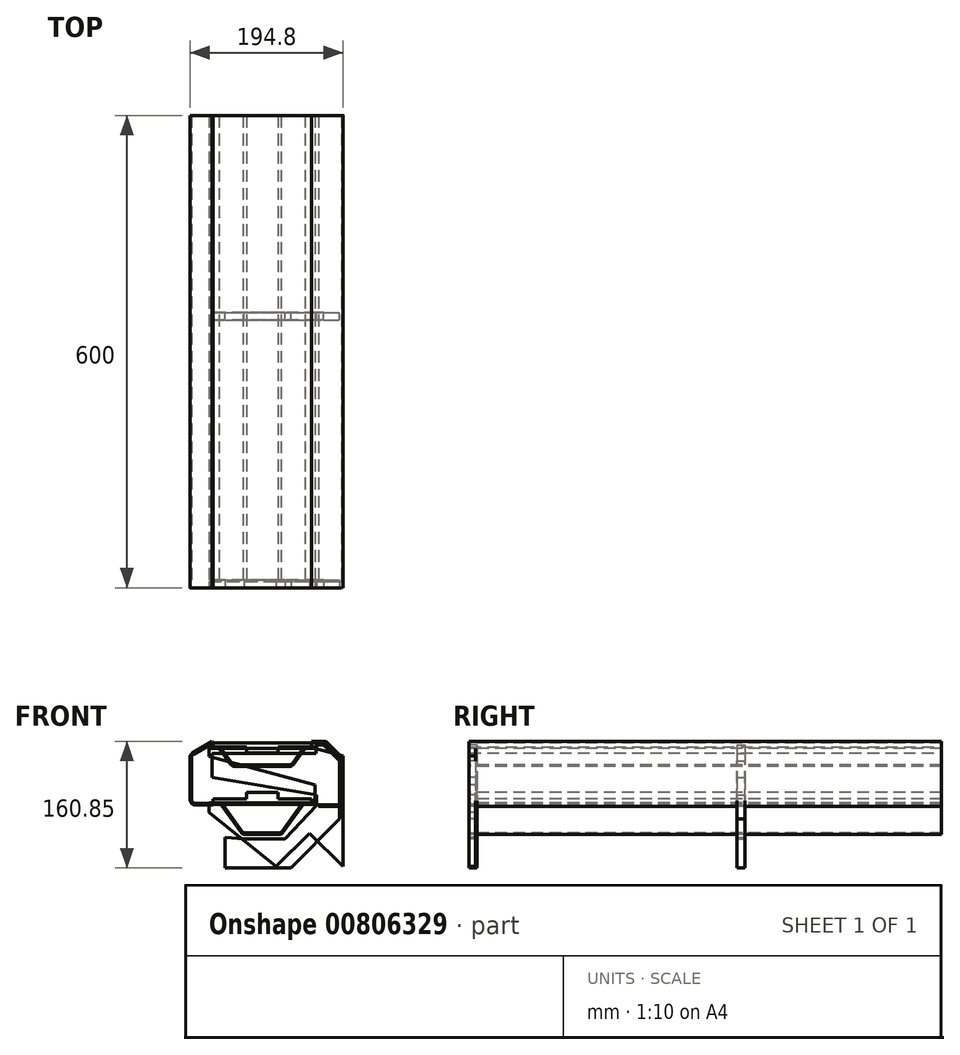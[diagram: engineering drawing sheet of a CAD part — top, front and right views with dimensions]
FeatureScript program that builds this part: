
annotation { "Feature Type Name" : "Feature", "Feature Type Description" : "" }
export const myFeature = defineFeature(function(context is Context, id is Id, definition is map)
    precondition{}
    {
        {
            var Q0;
            Q0=qCreatedBy(makeId("Front.planeOp"),FACE);
            var sketch = newSketch(context, id + "F0", { "sketchPlane" : qUnion([Q0])});
            skLineSegment(sketch, "E0.bottom", {"start": v(62.5, 2.5) * mm, "end": v(-62.5, 2.5) * mm});
            skLineSegment(sketch, "E0.top", {"start": v(62.5, -2.5) * mm, "end": v(20, -2.5) * mm});
            skLineSegment(sketch, "E0.left", {"start": v(62.5, 2.5) * mm, "end": v(62.5, -2.5) * mm});
            skLineSegment(sketch, "E0.right", {"start": v(-62.5, 2.5) * mm, "end": v(-62.5, -2.5) * mm});
            skPoint(sketch, "E0.middle", {"position": v(0, 0) * mm});
            skLineSegment(sketch, "E1.top", {"start": v(20, -10.5) * mm, "end": v(-20, -10.5) * mm});
            skLineSegment(sketch, "E1.left", {"start": v(20, -2.5) * mm, "end": v(20, -10.5) * mm});
            skLineSegment(sketch, "E1.right", {"start": v(-20, -2.5) * mm, "end": v(-20, -10.5) * mm});
            skPoint(sketch, "E1.middle", {"position": v(0, -6.5) * mm});
            skLineSegment(sketch, "E2.trimOffspring", {"start": v(-20, -2.5) * mm, "end": v(-62.5, -2.5) * mm});
            skSolve(sketch);
        }
        {
            var Q0;
            Q0 = qSketchRegion(id + "F0", true);
            extrude(context, id + "F1", {"entities" : qUnion([Q0]), "depth" : 600 * mm, "offsetDistance" : 25 * mm});
        }
        {
            var Q0;
            Q0=makeQuery(id+"F1.opExtrude","CAP_FACE",FACE,{"disambiguationData":[OSD([sQuery(id+"F0.wireOp",EDGE,"E0.bottom"),sQuery(id+"F0.wireOp",EDGE,"E0.top"),sQuery(id+"F0.wireOp",EDGE,"E0.left"),sQuery(id+"F0.wireOp",EDGE,"E0.right"),sQuery(id+"F0.wireOp",EDGE,"E1.top"),sQuery(id+"F0.wireOp",EDGE,"E1.left"),sQuery(id+"F0.wireOp",EDGE,"E1.right"),sQuery(id+"F0.wireOp",EDGE,"E2.trimOffspring")])],"isStart":false});
            var sketch = newSketch(context, id + "F2", { "sketchPlane" : qUnion([Q0])});
            skLineSegment(sketch, "E3.bottom", {"start": v(62.5, -68.5) * mm, "end": v(-62.5, -68.5) * mm});
            skLineSegment(sketch, "E3.top", {"start": v(62.5, -73.5) * mm, "end": v(-62.5, -73.5) * mm});
            skLineSegment(sketch, "E3.left", {"start": v(62.5, -68.5) * mm, "end": v(62.5, -73.5) * mm});
            skLineSegment(sketch, "E3.right", {"start": v(-62.5, -68.5) * mm, "end": v(-62.5, -73.5) * mm});
            skPoint(sketch, "E3.middle", {"position": v(0, -71) * mm});
            skLineSegment(sketch, "E4.bottom", {"start": v(20, -68.5) * mm, "end": v(-20, -68.5) * mm});
            skLineSegment(sketch, "E4.top", {"start": v(20, -60.5) * mm, "end": v(-20, -60.5) * mm});
            skLineSegment(sketch, "E4.left", {"start": v(20, -68.5) * mm, "end": v(20, -60.5) * mm});
            skLineSegment(sketch, "E4.right", {"start": v(-20, -68.5) * mm, "end": v(-20, -60.5) * mm});
            skPoint(sketch, "E4.middle", {"position": v(0, -64.5) * mm});
            skSolve(sketch);
        }
        {
            var Q0;
            Q0 = qSketchRegion(id + "F2", true);
            extrude(context, id + "F3", {"entities" : qUnion([Q0]), "oppositeDirection" : true, "depth" : 600 * mm, "offsetDistance" : 25 * mm});
        }
        {
            var Q0;
            Q0=makeQuery(id+"F3.opExtrude","CAP_FACE",FACE,{"disambiguationData":[OSD([sQuery(id+"F2.wireOp",EDGE,"E3.bottom"),sQuery(id+"F2.wireOp",EDGE,"E3.top"),sQuery(id+"F2.wireOp",EDGE,"E3.left"),sQuery(id+"F2.wireOp",EDGE,"E3.right"),sQuery(id+"F2.wireOp",EDGE,"E4.top"),sQuery(id+"F2.wireOp",EDGE,"E4.left"),sQuery(id+"F2.wireOp",EDGE,"E4.right")])],"isStart":true});
            var sketch = newSketch(context, id + "F4", { "sketchPlane" : qUnion([Q0])});
            skLineSegment(sketch, "E5", {"start": v(-67.5, -4.5) * mm, "end": v(-67.5, -14.5) * mm});
            skLineSegment(sketch, "E6", {"start": v(-67.5, -14.5) * mm, "end": v(67.5, -50.67) * mm});
            skLineSegment(sketch, "E7", {"start": v(-67.5, -75.5) * mm, "end": v(-67.5, -85.5) * mm});
            skLineSegment(sketch, "E8", {"start": v(67.5, -75.5) * mm, "end": v(67.5, -50.67) * mm});
            skLineSegment(sketch, "E9", {"start": v(-67.5, -75.5) * mm, "end": v(67.5, -75.5) * mm});
            skLineSegment(sketch, "E10", {"start": v(-67.5, -4.5) * mm, "end": v(67.5, -4.5) * mm});
            skLineSegment(sketch, "E11", {"start": v(67.5, -4.5) * mm, "end": v(102.5, -13.88) * mm});
            skCircle(sketch, "E12.cCircle", {"center": v(60.07, -154.62) * mm, "radius": 30 * mm, "construction": true});
            skLineSegment(sketch, "E12.0", {"start": v(17.65, -154.62) * mm, "end": v(60.07, -112.2) * mm});
            skLineSegment(sketch, "E12.1", {"start": v(60.07, -112.2) * mm, "end": v(102.5, -154.62) * mm});
            skLineSegment(sketch, "E12.2", {"start": v(102.5, -154.62) * mm, "end": v(60.07, -197.05) * mm});
            skLineSegment(sketch, "E12.3", {"start": v(60.07, -197.05) * mm, "end": v(17.65, -154.62) * mm});
            skPoint(sketch, "E12.0.midPoint", {"position": v(38.86, -133.41) * mm});
            skLineSegment(sketch, "E13", {"start": v(102.5, -13.88) * mm, "end": v(102.5, -154.62) * mm});
            skLineSegment(sketch, "E14", {"start": v(17.65, -154.62) * mm, "end": v(-67.5, -85.5) * mm});
            skSolve(sketch);
        }
        {
            var Q0;
            Q0=makeQuery(id+"F4.imprint","IMPRINT",FACE,{"disambiguationData":[TD([[makeQuery(id+"F4.imprint","IMPRINT",EDGE,{"derivedFrom":sQuery(id+"F4.wireOp",EDGE,"E5")}),1.0]])]});
            extrude(context, id + "F5", {"entities" : qUnion([Q0]), "oppositeDirection" : true, "depth" : 8 * mm, "offsetDistance" : 25 * mm});
        }
        {
            var Q0;
            Q0=makeQuery(id+"F3.opExtrude","CAP_FACE",FACE,{"disambiguationData":[OSD([sQuery(id+"F2.wireOp",EDGE,"E3.bottom"),sQuery(id+"F2.wireOp",EDGE,"E3.top"),sQuery(id+"F2.wireOp",EDGE,"E3.left"),sQuery(id+"F2.wireOp",EDGE,"E3.right"),sQuery(id+"F2.wireOp",EDGE,"E4.top"),sQuery(id+"F2.wireOp",EDGE,"E4.left"),sQuery(id+"F2.wireOp",EDGE,"E4.right")])],"isStart":true});
            var sketch = newSketch(context, id + "F6", { "sketchPlane" : qUnion([Q0])});
            skLineSegment(sketch, "E15", {"start": v(-67.5, -73.5) * mm, "end": v(-67.5, -75.5) * mm});
            skLineSegment(sketch, "E16", {"start": v(-67.5, -75.5) * mm, "end": v(-54.54, -75.5) * mm});
            skLineSegment(sketch, "E17", {"start": v(-51.3, -77.15) * mm, "end": v(-26.2, -111.85) * mm});
            skLineSegment(sketch, "E18", {"start": v(-22.96, -113.5) * mm, "end": v(0, -113.5) * mm});
            skLineSegment(sketch, "E19", {"start": v(0, -113.5) * mm, "end": v(0, -98.02) * mm, "construction": true});
            skLineSegment(sketch, "E20.MirrorCS", {"start": v(67.5, -73.5) * mm, "end": v(67.5, -75.5) * mm});
            skLineSegment(sketch, "E21.MirrorCS", {"start": v(67.5, -75.5) * mm, "end": v(54.54, -75.5) * mm});
            skLineSegment(sketch, "E22.MirrorCS", {"start": v(51.3, -77.15) * mm, "end": v(26.2, -111.85) * mm});
            skLineSegment(sketch, "E23.MirrorCS", {"start": v(22.96, -113.5) * mm, "end": v(0, -113.5) * mm});
            skPoint(sketch, "E24.visualSharp", {"position": v(-25, -113.5) * mm});
            skArc(sketch, "E24.filletArc", {"start": v(-26.2, -111.85) * mm, "mid": v(-24.78, -113.06) * mm, "end": v(-22.96, -113.5) * mm});
            skPoint(sketch, "E25.visualSharp", {"position": v(25, -113.5) * mm});
            skArc(sketch, "E25.filletArc", {"start": v(22.96, -113.5) * mm, "mid": v(24.78, -113.06) * mm, "end": v(26.2, -111.85) * mm});
            skPoint(sketch, "E26.visualSharp", {"position": v(52.5, -75.5) * mm});
            skArc(sketch, "E26.filletArc", {"start": v(54.54, -75.5) * mm, "mid": v(52.72, -75.94) * mm, "end": v(51.3, -77.15) * mm});
            skPoint(sketch, "E27.visualSharp", {"position": v(-52.5, -75.5) * mm});
            skArc(sketch, "E27.filletArc", {"start": v(-51.3, -77.15) * mm, "mid": v(-52.72, -75.94) * mm, "end": v(-54.54, -75.5) * mm});
            skLineSegment(sketch, "E28.0", {"start": v(-23.98, -111.5) * mm, "end": v(0, -111.5) * mm});
            skLineSegment(sketch, "E28.1", {"start": v(-49.68, -75.98) * mm, "end": v(-23.98, -111.5) * mm});
            skArc(sketch, "E28.2", {"start": v(-49.68, -75.98) * mm, "mid": v(-51.81, -74.16) * mm, "end": v(-54.54, -73.5) * mm});
            skLineSegment(sketch, "E28.3", {"start": v(-67.5, -73.5) * mm, "end": v(-54.54, -73.5) * mm});
            skLineSegment(sketch, "E29.0", {"start": v(23.98, -111.5) * mm, "end": v(0, -111.5) * mm});
            skLineSegment(sketch, "E29.1", {"start": v(49.68, -75.98) * mm, "end": v(23.98, -111.5) * mm});
            skArc(sketch, "E29.2", {"start": v(54.54, -73.5) * mm, "mid": v(51.81, -74.16) * mm, "end": v(49.68, -75.98) * mm});
            skLineSegment(sketch, "E29.3", {"start": v(67.5, -73.5) * mm, "end": v(54.54, -73.5) * mm});
            skPoint(sketch, "E30.orphan", {"position": v(67.5, -72.5) * mm});
            skPoint(sketch, "E31.orphan", {"position": v(-67.5, -72.5) * mm});
            skSolve(sketch);
        }
        {
            var Q0;
            {var subQ1=sQuery(id+"F6.wireOp",EDGE,"E15");Q0=makeQuery(id+"F6.imprint","IMPRINT",FACE,{"disambiguationData":[TD([[makeQuery(id+"F6.imprint","IMPRINT",EDGE,{"derivedFrom":subQ1}),1.0]])]});}
            extrude(context, id + "F7", {"entities" : qUnion([Q0]), "oppositeDirection" : true, "depth" : 600 * mm, "offsetDistance" : 25 * mm});
        }
        {
            var Q0;
            Q0=makeQuery(id+"F3.opExtrude","CAP_FACE",FACE,{"disambiguationData":[OSD([sQuery(id+"F2.wireOp",EDGE,"E3.bottom"),sQuery(id+"F2.wireOp",EDGE,"E3.top"),sQuery(id+"F2.wireOp",EDGE,"E3.left"),sQuery(id+"F2.wireOp",EDGE,"E3.right"),sQuery(id+"F2.wireOp",EDGE,"E4.top"),sQuery(id+"F2.wireOp",EDGE,"E4.left"),sQuery(id+"F2.wireOp",EDGE,"E4.right")])],"isStart":true});
            var sketch = newSketch(context, id + "F8", { "sketchPlane" : qUnion([Q0])});
            skLineSegment(sketch, "E32", {"start": v(-67.5, -2.5) * mm, "end": v(-56.04, -2.5) * mm});
            skLineSegment(sketch, "E33", {"start": v(-51.99, -4.57) * mm, "end": v(-38.34, -23.43) * mm});
            skLineSegment(sketch, "E34", {"start": v(-34.29, -25.5) * mm, "end": v(0, -25.5) * mm});
            skLineSegment(sketch, "E35", {"start": v(0, -25.5) * mm, "end": v(0, -6.97) * mm, "construction": true});
            skLineSegment(sketch, "E36.MirrorCS", {"start": v(34.29, -25.5) * mm, "end": v(0, -25.5) * mm});
            skLineSegment(sketch, "E37.MirrorCS", {"start": v(67.5, -2.5) * mm, "end": v(56.04, -2.5) * mm});
            skLineSegment(sketch, "E38.MirrorCS", {"start": v(51.99, -4.57) * mm, "end": v(38.34, -23.43) * mm});
            skPoint(sketch, "E39.visualSharp", {"position": v(-53.48, -2.5) * mm});
            skArc(sketch, "E39.filletArc", {"start": v(-51.99, -4.57) * mm, "mid": v(-53.76, -3.05) * mm, "end": v(-56.04, -2.5) * mm});
            skPoint(sketch, "E40.visualSharp", {"position": v(-36.84, -25.5) * mm});
            skArc(sketch, "E40.filletArc", {"start": v(-38.34, -23.43) * mm, "mid": v(-36.56, -24.95) * mm, "end": v(-34.29, -25.5) * mm});
            skPoint(sketch, "E41.visualSharp", {"position": v(36.84, -25.5) * mm});
            skArc(sketch, "E41.filletArc", {"start": v(34.29, -25.5) * mm, "mid": v(36.56, -24.95) * mm, "end": v(38.34, -23.43) * mm});
            skPoint(sketch, "E42.visualSharp", {"position": v(53.48, -2.5) * mm});
            skArc(sketch, "E42.filletArc", {"start": v(56.04, -2.5) * mm, "mid": v(53.76, -3.05) * mm, "end": v(51.99, -4.57) * mm});
            skArc(sketch, "E43.0", {"start": v(-39.96, -24.6) * mm, "mid": v(-37.47, -26.73) * mm, "end": v(-34.29, -27.5) * mm});
            skLineSegment(sketch, "E43.1", {"start": v(-54.5, -4.5) * mm, "end": v(-39.96, -24.6) * mm});
            skLineSegment(sketch, "E43.2", {"start": v(-67.5, -4.5) * mm, "end": v(-54.5, -4.5) * mm});
            skLineSegment(sketch, "E44.0", {"start": v(67.5, -4.5) * mm, "end": v(54.5, -4.5) * mm});
            skLineSegment(sketch, "E44.1", {"start": v(-34.29, -27.5) * mm, "end": v(0, -27.5) * mm});
            skLineSegment(sketch, "E44.2", {"start": v(34.29, -27.5) * mm, "end": v(0, -27.5) * mm});
            skArc(sketch, "E44.3", {"start": v(34.29, -27.5) * mm, "mid": v(37.47, -26.73) * mm, "end": v(39.96, -24.6) * mm});
            skLineSegment(sketch, "E44.4", {"start": v(54.5, -4.5) * mm, "end": v(39.96, -24.6) * mm});
            skLineSegment(sketch, "E45", {"start": v(-67.5, -4.5) * mm, "end": v(-67.5, -2.5) * mm});
            skLineSegment(sketch, "E46", {"start": v(67.5, -2.5) * mm, "end": v(67.5, -4.5) * mm});
            skSolve(sketch);
        }
        {
            var Q0;
            Q0 = qSketchRegion(id + "F8", true);
            extrude(context, id + "F9", {"entities" : qUnion([Q0]), "oppositeDirection" : true, "depth" : 600 * mm, "offsetDistance" : 25 * mm});
        }
        {
            var Q0;
            Q0=makeQuery(id+"F1.opExtrude","CAP_FACE",FACE,{"disambiguationData":[OSD([sQuery(id+"F0.wireOp",EDGE,"E0.bottom"),sQuery(id+"F0.wireOp",EDGE,"E0.top"),sQuery(id+"F0.wireOp",EDGE,"E0.left"),sQuery(id+"F0.wireOp",EDGE,"E0.right"),sQuery(id+"F0.wireOp",EDGE,"E1.top"),sQuery(id+"F0.wireOp",EDGE,"E1.left"),sQuery(id+"F0.wireOp",EDGE,"E1.right"),sQuery(id+"F0.wireOp",EDGE,"E2.trimOffspring")])],"isStart":false});
            var sketch = newSketch(context, id + "F10", { "sketchPlane" : qUnion([Q0])});
            skLineSegment(sketch, "E47", {"start": v(69.07, -63.4) * mm, "end": v(69.07, -77.09) * mm});
            skLineSegment(sketch, "E48", {"start": v(69.07, -77.09) * mm, "end": v(28.97, -119.72) * mm});
            skLineSegment(sketch, "E49", {"start": v(28.97, -119.72) * mm, "end": v(-23.25, -119.72) * mm});
            skLineSegment(sketch, "E50", {"start": v(-47.14, -117.81) * mm, "end": v(-23.25, -119.72) * mm});
            skLineSegment(sketch, "E51", {"start": v(-47.14, -117.81) * mm, "end": v(-47.14, -156.35) * mm});
            skLineSegment(sketch, "E52", {"start": v(-47.14, -156.35) * mm, "end": v(36.65, -156.35) * mm});
            skLineSegment(sketch, "E53", {"start": v(36.65, -156.35) * mm, "end": v(98.6, -94.32) * mm});
            skLineSegment(sketch, "E54", {"start": v(98.6, -94.32) * mm, "end": v(98.6, -20.5) * mm});
            skLineSegment(sketch, "E55", {"start": v(78.11, 0) * mm, "end": v(68.96, 0) * mm});
            skLineSegment(sketch, "E56", {"start": v(68.73, -10.7) * mm, "end": v(-63.58, -10.7) * mm});
            skLineSegment(sketch, "E57", {"start": v(-63.58, -10.7) * mm, "end": v(-63.58, -41.24) * mm});
            skLineSegment(sketch, "E58", {"start": v(-63.58, -41.24) * mm, "end": v(69.07, -63.4) * mm});
            skPoint(sketch, "E59.orphan", {"position": v(69.07, -49.7) * mm});
            skLineSegment(sketch, "E60", {"start": v(68.96, 0) * mm, "end": v(68.73, -10.7) * mm});
            skLineSegment(sketch, "E61", {"start": v(78.11, 0) * mm, "end": v(98.6, -20.5) * mm});
            skPoint(sketch, "E62.orphan", {"position": v(98.6, 0) * mm});
            skSolve(sketch);
        }
        {
            var Q0;
            Q0 = qSketchRegion(id + "F10", true);
            extrude(context, id + "F11", {"entities" : qUnion([Q0]), "oppositeDirection" : true, "depth" : 10 * mm, "offsetDistance" : 25 * mm});
        }
        {
            var Q0;
            Q0=makeQuery(id+"F11.opExtrude","CAP_FACE",FACE,{"disambiguationData":[OSD([sQuery(id+"F10.wireOp",EDGE,"E47"),sQuery(id+"F10.wireOp",EDGE,"E48"),sQuery(id+"F10.wireOp",EDGE,"E49"),sQuery(id+"F10.wireOp",EDGE,"E50"),sQuery(id+"F10.wireOp",EDGE,"E51"),sQuery(id+"F10.wireOp",EDGE,"E52"),sQuery(id+"F10.wireOp",EDGE,"E53"),sQuery(id+"F10.wireOp",EDGE,"E54"),sQuery(id+"F10.wireOp",EDGE,"E55"),sQuery(id+"F10.wireOp",EDGE,"E56"),sQuery(id+"F10.wireOp",EDGE,"E57"),sQuery(id+"F10.wireOp",EDGE,"E58"),sQuery(id+"F10.wireOp",EDGE,"E60")])],"isStart":true});
            cPlane(context, id + "F12", {"entities" : qUnion([Q0]), "cplaneType" : CPlaneType.OFFSET, "offset" : 350 * mm, "oppositeDirection" : true, "width" : 150 * mm, "height" : 150 * mm});
        }
        {
            var Q0;
            Q0=qCreatedBy(id+"F12.planeOp",FACE);
            var sketch = newSketch(context, id + "F13", { "sketchPlane" : qUnion([Q0])});
            skLineSegment(sketch, "E63.0.0", {"start": v(68.73, -10.7) * mm, "end": v(-63.58, -10.7) * mm});
            skLineSegment(sketch, "E63.0.1", {"start": v(-63.58, -10.7) * mm, "end": v(-63.58, -41.24) * mm});
            skLineSegment(sketch, "E63.0.2", {"start": v(-63.58, -41.24) * mm, "end": v(69.07, -63.4) * mm});
            skLineSegment(sketch, "E63.0.3", {"start": v(69.07, -63.4) * mm, "end": v(69.07, -77.09) * mm});
            skLineSegment(sketch, "E63.0.4", {"start": v(69.07, -77.09) * mm, "end": v(28.97, -119.72) * mm});
            skLineSegment(sketch, "E63.0.5", {"start": v(28.97, -119.72) * mm, "end": v(-23.25, -119.72) * mm});
            skLineSegment(sketch, "E63.0.6", {"start": v(-23.25, -119.72) * mm, "end": v(-47.14, -117.81) * mm});
            skLineSegment(sketch, "E63.0.7", {"start": v(-47.14, -117.81) * mm, "end": v(-47.14, -156.35) * mm});
            skLineSegment(sketch, "E63.0.8", {"start": v(-47.14, -156.35) * mm, "end": v(36.65, -156.35) * mm});
            skLineSegment(sketch, "E63.0.9", {"start": v(36.65, -156.35) * mm, "end": v(98.6, -94.32) * mm});
            skLineSegment(sketch, "E63.0.10", {"start": v(98.6, -94.32) * mm, "end": v(98.6, -94.32) * mm});
            skLineSegment(sketch, "E63.0.11", {"start": v(78.11, 0) * mm, "end": v(68.96, 0) * mm});
            skLineSegment(sketch, "E63.0.12", {"start": v(68.96, 0) * mm, "end": v(68.73, -10.7) * mm});
            skLineSegment(sketch, "E64.0", {"start": v(78.11, 0) * mm, "end": v(98.6, -20.5) * mm});
            skLineSegment(sketch, "E65.0", {"start": v(98.6, -94.32) * mm, "end": v(98.6, -20.5) * mm});
            skSolve(sketch);
        }
        {
            var Q0;
            Q0 = qSketchRegion(id + "F13", true);
            extrude(context, id + "F14", {"entities" : qUnion([Q0]), "depth" : 10 * mm, "offsetDistance" : 25 * mm});
        }
        {
            var Q0;
            Q0=makeQuery(id+"F1.opExtrude","CAP_FACE",FACE,{"disambiguationData":[OSD([sQuery(id+"F0.wireOp",EDGE,"E0.bottom"),sQuery(id+"F0.wireOp",EDGE,"E0.top"),sQuery(id+"F0.wireOp",EDGE,"E0.left"),sQuery(id+"F0.wireOp",EDGE,"E0.right"),sQuery(id+"F0.wireOp",EDGE,"E1.top"),sQuery(id+"F0.wireOp",EDGE,"E1.left"),sQuery(id+"F0.wireOp",EDGE,"E1.right"),sQuery(id+"F0.wireOp",EDGE,"E2.trimOffspring")])],"isStart":false});
            var sketch = newSketch(context, id + "F15", { "sketchPlane" : qUnion([Q0])});
            skLineSegment(sketch, "E66", {"start": v(62.5, 2.5) * mm, "end": v(78.84, 2.27) * mm});
            skLineSegment(sketch, "E67", {"start": v(82.35, 0.77) * mm, "end": v(99.57, -16.89) * mm});
            skLineSegment(sketch, "E68", {"start": v(101, -20.38) * mm, "end": v(101, -70.98) * mm});
            skPoint(sketch, "E69.visualSharp", {"position": v(80.9, 2.25) * mm});
            skArc(sketch, "E69.filletArc", {"start": v(82.35, 0.77) * mm, "mid": v(80.75, 1.87) * mm, "end": v(78.84, 2.27) * mm});
            skPoint(sketch, "E70.visualSharp", {"position": v(101, -18.34) * mm});
            skArc(sketch, "E70.filletArc", {"start": v(101, -20.38) * mm, "mid": v(100.62, -18.5) * mm, "end": v(99.57, -16.89) * mm});
            skLineSegment(sketch, "E71.2", {"start": v(103, -20.38) * mm, "end": v(103, -70.98) * mm});
            skLineSegment(sketch, "E71.3", {"start": v(62.53, 4.5) * mm, "end": v(78.87, 4.27) * mm});
            skArc(sketch, "E71.4", {"start": v(83.78, 2.16) * mm, "mid": v(81.54, 3.7) * mm, "end": v(78.87, 4.27) * mm});
            skLineSegment(sketch, "E71.5", {"start": v(83.78, 2.16) * mm, "end": v(101, -15.5) * mm});
            skArc(sketch, "E71.6", {"start": v(103, -20.38) * mm, "mid": v(102.48, -17.74) * mm, "end": v(101, -15.5) * mm});
            skLineSegment(sketch, "E72", {"start": v(62.5, 2.5) * mm, "end": v(62.53, 4.5) * mm});
            skLineSegment(sketch, "E73", {"start": v(96, -75.98) * mm, "end": v(71.34, -75.98) * mm});
            skLineSegment(sketch, "E74", {"start": v(71.34, -75.98) * mm, "end": v(71.34, -77.98) * mm});
            skLineSegment(sketch, "E75", {"start": v(71.34, -77.98) * mm, "end": v(96, -77.98) * mm});
            skPoint(sketch, "E76.visualSharp", {"position": v(101, -75.98) * mm});
            skArc(sketch, "E76.filletArc", {"start": v(96, -75.98) * mm, "mid": v(99.53, -74.51) * mm, "end": v(101, -70.98) * mm});
            skPoint(sketch, "E77.visualSharp", {"position": v(103, -77.98) * mm});
            skArc(sketch, "E77.filletArc", {"start": v(96, -77.98) * mm, "mid": v(100.94, -75.93) * mm, "end": v(103, -70.98) * mm});
            skSolve(sketch);
        }
        {
            var Q0;
            Q0 = qSketchRegion(id + "F15", true);
            extrude(context, id + "F16", {"entities" : qUnion([Q0]), "oppositeDirection" : true, "depth" : 600 * mm, "offsetDistance" : 25 * mm});
        }
        {
            var Q0;
            Q0=makeQuery(id+"F1.opExtrude","CAP_FACE",FACE,{"disambiguationData":[OSD([sQuery(id+"F0.wireOp",EDGE,"E0.bottom"),sQuery(id+"F0.wireOp",EDGE,"E0.top"),sQuery(id+"F0.wireOp",EDGE,"E0.left"),sQuery(id+"F0.wireOp",EDGE,"E0.right"),sQuery(id+"F0.wireOp",EDGE,"E1.top"),sQuery(id+"F0.wireOp",EDGE,"E1.left"),sQuery(id+"F0.wireOp",EDGE,"E1.right"),sQuery(id+"F0.wireOp",EDGE,"E2.trimOffspring")])],"isStart":false});
            var sketch = newSketch(context, id + "F17", { "sketchPlane" : qUnion([Q0])});
            skLineSegment(sketch, "E78", {"start": v(-62.5, 2.5) * mm, "end": v(-87.33, -12) * mm});
            skLineSegment(sketch, "E79", {"start": v(-89.8, -16.31) * mm, "end": v(-89.8, -69.3) * mm});
            skLineSegment(sketch, "E80", {"start": v(-84.8, -74.3) * mm, "end": v(-62.2, -74.3) * mm});
            skPoint(sketch, "E81.visualSharp", {"position": v(-89.8, -13.44) * mm});
            skArc(sketch, "E81.filletArc", {"start": v(-87.33, -12) * mm, "mid": v(-89.15, -13.82) * mm, "end": v(-89.8, -16.31) * mm});
            skPoint(sketch, "E82.visualSharp", {"position": v(-89.8, -74.3) * mm});
            skArc(sketch, "E82.filletArc", {"start": v(-89.8, -69.3) * mm, "mid": v(-88.34, -72.83) * mm, "end": v(-84.8, -74.3) * mm});
            skLineSegment(sketch, "E83.0", {"start": v(-84.8, -76.3) * mm, "end": v(-62.2, -76.3) * mm});
            skLineSegment(sketch, "E83.1", {"start": v(-63.5, 4.23) * mm, "end": v(-88.34, -10.27) * mm});
            skArc(sketch, "E83.2", {"start": v(-88.34, -10.27) * mm, "mid": v(-90.88, -12.83) * mm, "end": v(-91.8, -16.31) * mm});
            skLineSegment(sketch, "E83.3", {"start": v(-91.8, -16.31) * mm, "end": v(-91.8, -69.3) * mm});
            skArc(sketch, "E83.4", {"start": v(-91.8, -69.3) * mm, "mid": v(-89.76, -74.25) * mm, "end": v(-84.8, -76.3) * mm});
            skLineSegment(sketch, "E84", {"start": v(-63.5, 4.23) * mm, "end": v(-62.5, 2.5) * mm});
            skLineSegment(sketch, "E85", {"start": v(-62.2, -74.3) * mm, "end": v(-62.2, -76.3) * mm});
            skSolve(sketch);
        }
        {
            var Q0;
            Q0=makeQuery(id+"F17.imprint","IMPRINT",FACE,{"disambiguationData":[TD([[makeQuery(id+"F17.imprint","IMPRINT",EDGE,{"derivedFrom":sQuery(id+"F17.wireOp",EDGE,"E78")}),-1.0]])]});
            extrude(context, id + "F18", {"entities" : qUnion([Q0]), "oppositeDirection" : true, "depth" : 600 * mm, "offsetDistance" : 25 * mm});
        }
    });
